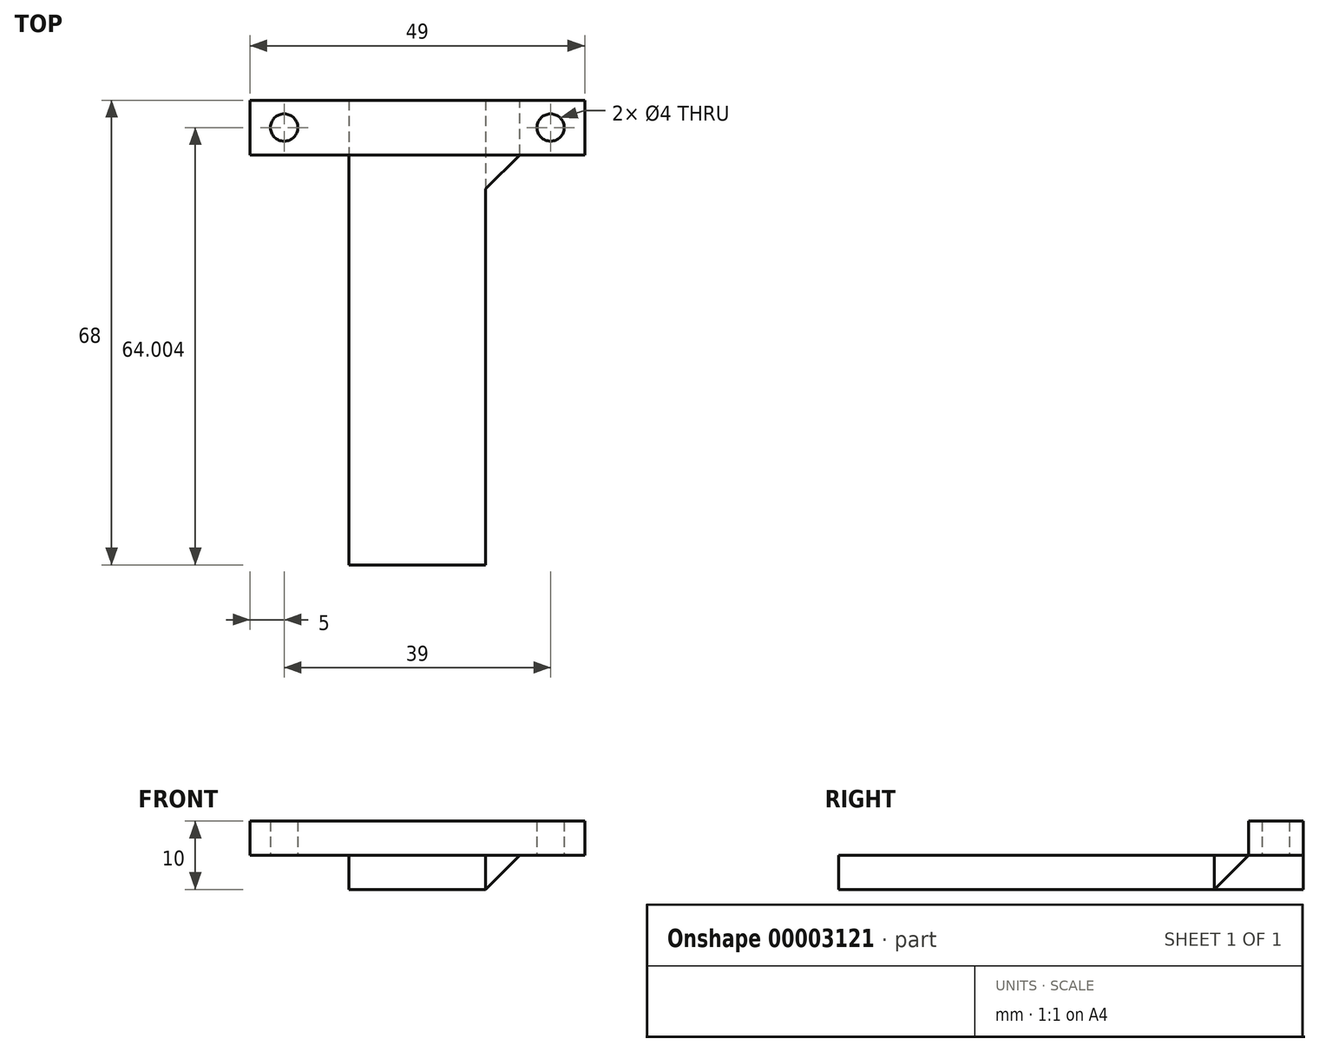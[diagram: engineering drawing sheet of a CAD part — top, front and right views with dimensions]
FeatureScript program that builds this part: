
annotation { "Feature Type Name" : "Feature", "Feature Type Description" : "" }
export const myFeature = defineFeature(function(context is Context, id is Id, definition is map)
    precondition{}
    {
        {
            var Q0;
            Q0=qCreatedBy(makeId("Top.planeOp"),FACE);
            var sketch = newSketch(context, id + "F0", { "sketchPlane" : qUnion([Q0])});
            skLineSegment(sketch, "E0.bottom", {"start": v(-49, 14.98) * mm, "end": v(0, 14.98) * mm});
            skLineSegment(sketch, "E0.top", {"start": v(-49, 6.98) * mm, "end": v(0, 6.98) * mm});
            skLineSegment(sketch, "E0.left", {"start": v(-49, 14.98) * mm, "end": v(-49, 6.98) * mm});
            skLineSegment(sketch, "E0.right", {"start": v(0, 14.98) * mm, "end": v(0, 6.98) * mm});
            skCircle(sketch, "E1", {"center": v(-44, 10.98) * mm, "radius": 2 * mm});
            skCircle(sketch, "E2", {"center": v(-5, 10.98) * mm, "radius": 2 * mm});
            skLineSegment(sketch, "E3", {"start": v(-49, 10.98) * mm, "end": v(0, 10.98) * mm, "construction": true});
            skLineSegment(sketch, "E4.bottom", {"start": v(-20.12, 14.98) * mm, "end": v(-9.76, 14.98) * mm});
            skLineSegment(sketch, "E4.top", {"start": v(-20.12, 6.98) * mm, "end": v(-9.76, 6.98) * mm});
            skLineSegment(sketch, "E5", {"start": v(-34.5, 14.98) * mm, "end": v(-34.5, 6.98) * mm});
            skLineSegment(sketch, "E6", {"start": v(-14.5, 14.98) * mm, "end": v(-14.5, 6.98) * mm});
            skLineSegment(sketch, "E7", {"start": v(-24.5, 6.98) * mm, "end": v(-24.5, 14.98) * mm, "construction": true});
            skSolve(sketch);
        }
        {
            var Q0;
            {var subQ1=sQuery(id+"F0.wireOp",EDGE,"E0.left");Q0=makeQuery(id+"F0.imprint","IMPRINT",FACE,{"disambiguationData":[TD([[makeQuery(id+"F0.imprint","IMPRINT",EDGE,{"derivedFrom":subQ1}),1.0]])]});}
            var Q1;
            Q1=makeQuery(id+"F0.imprint","IMPRINT",FACE,{"disambiguationData":[TD([[makeQuery(id+"F0.imprint","IMPRINT",EDGE,{"derivedFrom":sQuery(id+"F0.wireOp",EDGE,"E4.bottom")}),-1.0]])]});
            var Q2;
            {var subQ1=sQuery(id+"F0.wireOp",EDGE,"E0.right");Q2=makeQuery(id+"F0.imprint","IMPRINT",FACE,{"disambiguationData":[TD([[makeQuery(id+"F0.imprint","IMPRINT",EDGE,{"derivedFrom":subQ1}),-1.0]])]});}
            var Q3;
            {var subQ1=sQuery(id+"F0.wireOp",EDGE,"E5");Q3=makeQuery(id+"F0.imprint","IMPRINT",FACE,{"disambiguationData":[TD([[makeQuery(id+"F0.imprint","IMPRINT",EDGE,{"derivedFrom":subQ1}),1.0]])]});}
            extrude(context, id + "F1", {"entities" : qUnion([Q0, Q1, Q2, Q3]), "depth" : 5 * mm});
        }
        {
            var Q0;
            Q0=makeQuery(id+"F0.imprint","IMPRINT",FACE,{"disambiguationData":[TD([[makeQuery(id+"F0.imprint","IMPRINT",EDGE,{"derivedFrom":sQuery(id+"F0.wireOp",EDGE,"E4.bottom")}),-1.0]])]});
            var Q1;
            {var subQ1=sQuery(id+"F0.wireOp",EDGE,"E5");Q1=makeQuery(id+"F0.imprint","IMPRINT",FACE,{"disambiguationData":[TD([[makeQuery(id+"F0.imprint","IMPRINT",EDGE,{"derivedFrom":subQ1}),1.0]])]});}
            extrude(context, id + "F2", {"entities" : qUnion([Q0, Q1]), "operationType" : NewBodyOperationType.ADD, "oppositeDirection" : true, "depth" : 5 * mm});
        }
        {
            var Q0;
            {var subQ0=sQuery(id+"F0.wireOp",EDGE,"E0.top");Q0=makeQuery(id+"F2.boolean.opBoolean","MERGE",FACE,{"derivedFrom":[makeQuery(id+"F1.opExtrude","SWEPT_FACE",FACE,{"disambiguationData":[OSD([subQ0,sQuery(id+"F0.wireOp",EDGE,"E4.top")])]}),makeQuery(id+"F2.opExtrude","SWEPT_FACE",FACE,{"disambiguationData":[OSD([subQ0])]})]});}
            var sketch = newSketch(context, id + "F3", { "sketchPlane" : qUnion([Q0])});
            skLineSegment(sketch, "E8", {"start": v(-34.5, 0) * mm, "end": v(-14.5, 0) * mm});
            skSolve(sketch);
        }
        {
            var Q0;
            Q0 = qSketchRegion(id + "F3", true);
            var Q1;
            Q1=makeQuery(id+"F3.imprint","IMPRINT",FACE,{"disambiguationData":[TD([[makeQuery(id+"F3.imprint","IMPRINT",EDGE,{"derivedFrom":sQuery(id+"F3.wireOp",EDGE,"E8")}),-1.0]])]});
            extrude(context, id + "F4", {"entities" : qUnion([Q0, Q1]), "operationType" : NewBodyOperationType.ADD, "depth" : 60 * mm});
        }
        {
            var Q0;
            Q0=makeQuery(id+"F2.opExtrude","CAP_EDGE",EDGE,{"disambiguationData":[OSD([sQuery(id+"F0.wireOp",EDGE,"E5")])],"isStart":true});
            var Q1;
            Q1=makeQuery(id+"F2.opExtrude","CAP_EDGE",EDGE,{"disambiguationData":[OSD([sQuery(id+"F0.wireOp",EDGE,"E6")])],"isStart":true});
            chamfer(context, id + "F5", {"entities" : qUnion([Q0, Q1]), "width" : 5 * mm, "tangentPropagation" : true});
        }
        {
            var Q0;
            {var subQ0=sQuery(id+"F0.wireOp",EDGE,"E0.top");var subQ1=sQuery(id+"F0.wireOp",EDGE,"E4.top");var subQ2=sQuery(id+"F0.wireOp",EDGE,"E6");Q0=makeQuery(id+"F5.opChamfer","TWEAK_EDGE",EDGE,{"derivedFrom":[makeQuery(id+"F4.boolean.opBoolean","MERGE",VERTEX,{"derivedFrom":[makeQuery(id+"F2.opExtrude","CAP_VERTEX",VERTEX,{"disambiguationData":[OSD([subQ0,subQ1,subQ2])],"isStart":true}),makeQuery(id+"F4.opExtrude","CAP_VERTEX",VERTEX,{"disambiguationData":[OSD([subQ0,subQ1,subQ2,sQuery(id+"F3.wireOp",EDGE,"E8")])],"isStart":true})]})]});}
            var Q1;
            {var subQ0=sQuery(id+"F0.wireOp",EDGE,"E0.top");var subQ1=sQuery(id+"F0.wireOp",EDGE,"E5");Q1=makeQuery(id+"F5.opChamfer","TWEAK_EDGE",EDGE,{"derivedFrom":[makeQuery(id+"F4.boolean.opBoolean","MERGE",VERTEX,{"derivedFrom":[makeQuery(id+"F2.opExtrude","CAP_VERTEX",VERTEX,{"disambiguationData":[OSD([subQ0,subQ1])],"isStart":true}),makeQuery(id+"F4.opExtrude","CAP_VERTEX",VERTEX,{"disambiguationData":[OSD([subQ0,sQuery(id+"F0.wireOp",EDGE,"E4.top"),subQ1,sQuery(id+"F3.wireOp",EDGE,"E8")])],"isStart":true})]})]});}
            chamfer(context, id + "F6", {"entities" : qUnion([Q0, Q1]), "width" : 5 * mm, "tangentPropagation" : true});
        }
    });
